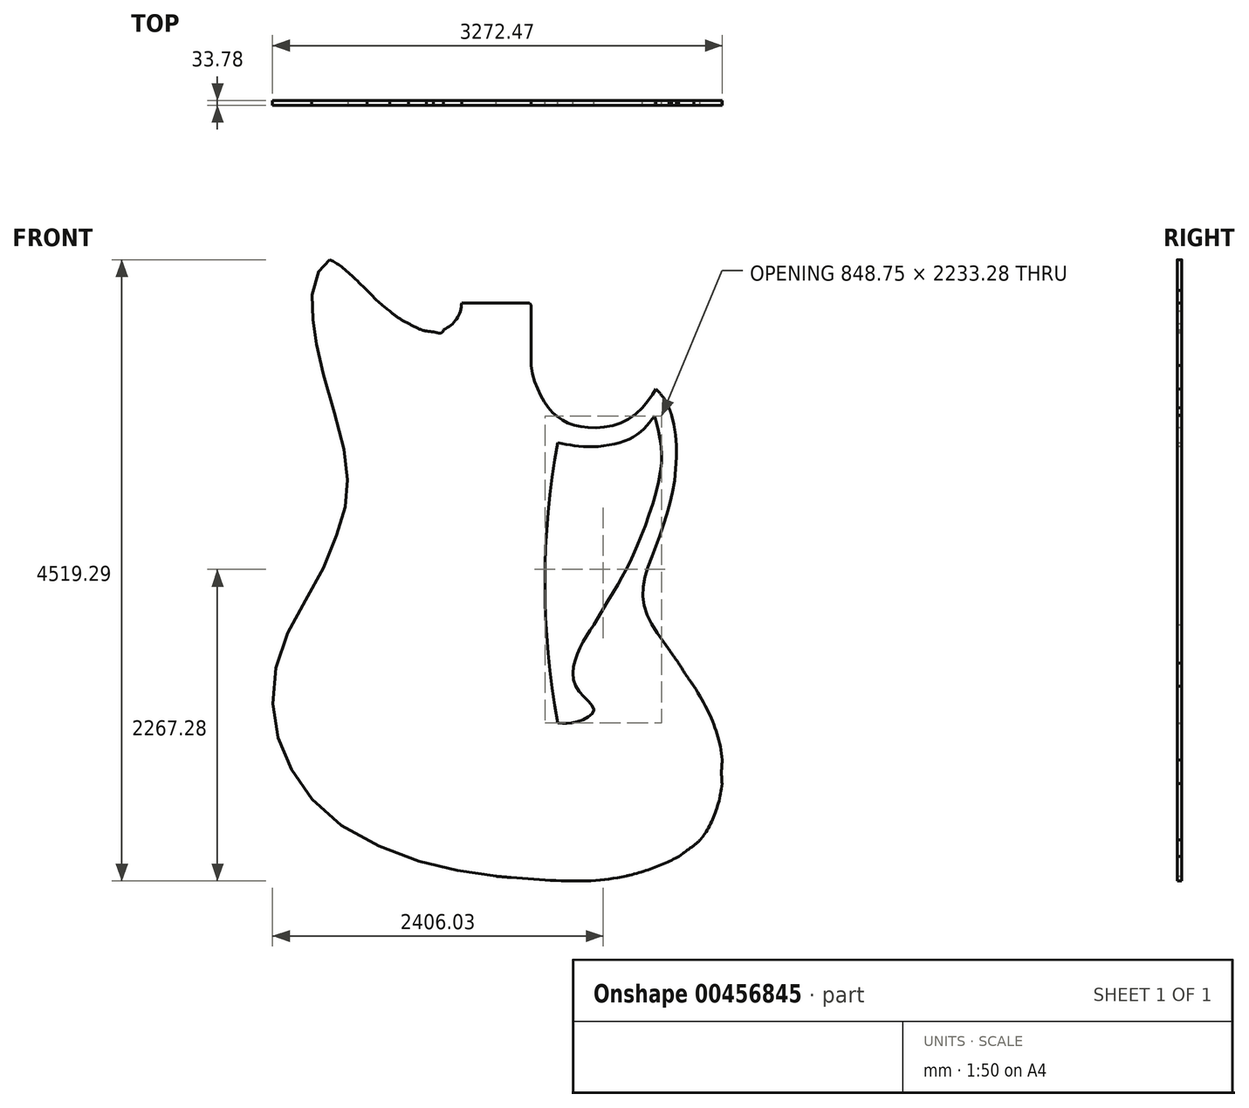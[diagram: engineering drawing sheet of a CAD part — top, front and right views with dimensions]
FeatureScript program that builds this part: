
annotation { "Feature Type Name" : "Feature", "Feature Type Description" : "" }
export const myFeature = defineFeature(function(context is Context, id is Id, definition is map)
    precondition{}
    {
        {
            var Q0;
            Q0=qCreatedBy(makeId("Front.planeOp"),FACE);
            var sketch = newSketch(context, id + "F0", { "sketchPlane" : qUnion([Q0])});
            skLineSegment(sketch, "E0", {"start": v(-6299.76, -3394.28) * mm, "end": v(-6299.76, -2656.01) * mm});
            skLineSegment(sketch, "E1", {"start": v(-6805.5, -2914.73) * mm, "end": v(-6805.5, -2630.61) * mm});
            skLineSegment(sketch, "E2", {"start": v(-6552.45, -2630.61) * mm, "end": v(-6552.45, -3394.86) * mm});
            skLineSegment(sketch, "E3", {"start": v(-6805.5, -3394.86) * mm, "end": v(-6805.5, -3072.04) * mm});
            skFitSpline(sketch, "E4", {"points": [v(-5276.05, -3449.11) * mm, v(-5287.3, -3419.3) * mm, v(-5308.03, -3364.3) * mm, v(-5355.3, -3290.17) * mm, v(-5416.6, -3231.95) * mm, v(-5491.73, -3195.94) * mm, v(-5588.2, -3145.91) * mm, v(-5719.98, -3168.37) * mm, v(-5802.47, -3218.14) * mm, v(-5845.07, -3228.05) * mm]});
            skFitSpline(sketch, "E5", {"points": [v(-5044.53, -6506.04) * mm, v(-5026.22, -6487.87) * mm, v(-4988.8, -6419.72) * mm, v(-4934.12, -6297.37) * mm, v(-4910.03, -6158) * mm, v(-4914.3, -6040.1) * mm, v(-4908, -5864.95) * mm, v(-4992.35, -5604.02) * mm, v(-5156.6, -5361.57) * mm, v(-5252.66, -5210.81) * mm, v(-5288.38, -5164.45) * mm]});
            skFitSpline(sketch, "E6", {"points": [v(-5582.6, -6794.39) * mm, v(-5525.91, -6781.71) * mm, v(-5422.3, -6758.55) * mm, v(-5280.26, -6694.9) * mm, v(-5158.48, -6609.42) * mm, v(-5078.14, -6546.43) * mm, v(-5044.53, -6506.04) * mm]});
            skFitSpline(sketch, "E7", {"points": [v(-6513.44, -6803.92) * mm, v(-6430.08, -6813.24) * mm, v(-6198.84, -6839.12) * mm, v(-5885.83, -6842.47) * mm, v(-5659.6, -6811.31) * mm, v(-5582.6, -6794.39) * mm]});
            skLineSegment(sketch, "E8", {"start": v(-6552.45, -6802.18) * mm, "end": v(-6552.45, -3394.86) * mm});
            skLineSegment(sketch, "E9", {"start": v(-6805.5, -3394.86) * mm, "end": v(-6299.4, -3394.86) * mm});
            skLineSegment(sketch, "E10", {"start": v(-6805.5, -3085.71) * mm, "end": v(-6829.62, -3072.04) * mm});
            skLineSegment(sketch, "E11", {"start": v(-6325.16, -2630.61) * mm, "end": v(-6805.5, -2630.61) * mm});
            skLineSegment(sketch, "E12", {"start": v(-6552.45, -3012.74) * mm, "end": v(-6552.45, -2630.61) * mm});
            skFitSpline(sketch, "E13", {"points": [v(-7676.8, -2286.7) * mm, v(-7695.14, -2283.28) * mm, v(-7735.83, -2290.19) * mm, v(-7763.38, -2317.11) * mm, v(-7777.56, -2329.88) * mm]});
            skFitSpline(sketch, "E14", {"points": [v(-6552.45, -6802.18) * mm, v(-7122.24, -6690.77) * mm, v(-7726.89, -6397.1) * mm, v(-8053.7, -6007.88) * mm, v(-8178.3, -5586.4) * mm, v(-8106.52, -5110.04) * mm, v(-7862.77, -4657.97) * mm, v(-7687.73, -4243.4) * mm, v(-7635.05, -3965.52) * mm, v(-7685.82, -3593.24) * mm, v(-7834.6, -3064.8) * mm, v(-7881.52, -2796.52) * mm, v(-7892.2, -2569.59) * mm, v(-7834.6, -2376.3) * mm, v(-7765.47, -2318.94) * mm, v(-7285.71, -2724.93) * mm, v(-7025.82, -2835.37) * mm, v(-6937.48, -2806.54) * mm, v(-6805.5, -2630.61) * mm], "startDerivative": vector(-8367.9, 1054.47) * mm, "endDerivative": vector(19439.29, -15558.9) * mm});
            skPoint(sketch, "E15.17.internal.snap0", {"position": v(-6254.8, -7225.1) * mm});
            skFitSpline(sketch, "E15", {"points": [v(-6552.45, -6802.18) * mm, v(-5969.39, -6837.11) * mm, v(-5582.6, -6794.39) * mm, v(-5249.83, -6671.29) * mm, v(-5044.53, -6506.04) * mm, v(-4915.92, -6170.56) * mm, v(-4928.43, -5832.38) * mm, v(-5044.53, -5540.75) * mm, v(-5288.38, -5164.45) * mm, v(-5485.93, -4796.16) * mm, v(-5390.99, -4398.41) * mm, v(-5254.92, -3911.55) * mm, v(-5276.05, -3449.11) * mm, v(-5391.06, -3257.77) * mm, v(-5558.7, -3166.06) * mm, v(-5784.71, -3206.46) * mm, v(-6012.82, -3259.28) * mm, v(-6254.8, -3158.3) * mm, v(-6296.95, -3091.35) * mm], "startDerivative": vector(8213.16, -709.74) * mm, "endDerivative": vector(-887.98, 2353.13) * mm});
            skFitSpline(sketch, "E16.trimOffspring", {"points": [v(-6552.45, -6802.18) * mm, v(-5969.39, -6837.11) * mm, v(-5582.6, -6794.39) * mm, v(-5249.83, -6671.29) * mm, v(-5044.53, -6506.04) * mm, v(-4915.92, -6170.56) * mm, v(-4928.43, -5832.38) * mm, v(-5044.53, -5540.75) * mm, v(-5288.38, -5164.45) * mm, v(-5485.93, -4796.16) * mm, v(-5390.99, -4398.41) * mm, v(-5254.92, -3911.55) * mm, v(-5276.05, -3449.11) * mm, v(-5391.06, -3257.77) * mm, v(-5558.7, -3166.06) * mm, v(-5784.71, -3206.46) * mm, v(-6012.82, -3259.28) * mm, v(-6254.8, -3158.3) * mm, v(-6296.95, -3091.35) * mm], "startDerivative": vector(8213.16, -709.74) * mm, "endDerivative": vector(-887.98, 2353.13) * mm});
            skFitSpline(sketch, "E17.trimOffspring", {"points": [v(-5044.53, -6506.04) * mm, v(-5026.22, -6487.87) * mm, v(-4988.8, -6419.72) * mm, v(-4934.12, -6297.37) * mm, v(-4910.03, -6158) * mm, v(-4914.3, -6040.1) * mm, v(-4908, -5864.95) * mm, v(-4992.35, -5604.02) * mm, v(-5156.6, -5361.57) * mm, v(-5252.66, -5210.81) * mm, v(-5288.38, -5164.45) * mm]});
            skArc(sketch, "E18.filletArc", {"start": v(-6813.35, -2920.9) * mm, "mid": v(-6807.93, -2919.72) * mm, "end": v(-6805.5, -2914.73) * mm});
            skArc(sketch, "E19", {"start": v(-7062, -2835.37) * mm, "mid": v(-6884.48, -2794.71) * mm, "end": v(-6805.5, -2630.61) * mm});
            skFitSpline(sketch, "E20", {"points": [v(-6299.76, -3085.86) * mm, v(-6209.62, -3342) * mm, v(-6080.38, -3479.85) * mm, v(-5890.06, -3537.13) * mm, v(-5592.72, -3477.35) * mm, v(-5391.06, -3257.77) * mm], "startDerivative": vector(186.4, -1403.01) * mm, "endDerivative": vector(492.18, 886.21) * mm});
            skArc(sketch, "E21.filletArc", {"start": v(-6299.76, -2656.01) * mm, "mid": v(-6307.2, -2638.05) * mm, "end": v(-6325.16, -2630.61) * mm});
            skFitSpline(sketch, "E22", {"points": [v(-7676.8, -2286.7) * mm, v(-7516.18, -2512.91) * mm, v(-7285.71, -2722.08) * mm, v(-7062, -2835.37) * mm], "startDerivative": vector(593.9, -835.52) * mm, "endDerivative": vector(356.24, -9.07) * mm});
            skFitSpline(sketch, "E23", {"points": [v(-5400.32, -3453.2) * mm, v(-5353.84, -3817.3) * mm, v(-5555.25, -4460.28) * mm, v(-5844.1, -4973.14) * mm], "startDerivative": vector(337.74, -1395.2) * mm, "endDerivative": vector(-1351.1, -2298.33) * mm});
            skFitSpline(sketch, "E24", {"points": [v(-5400.32, -3453.2) * mm, v(-5558.7, -3608.13) * mm, v(-5872.87, -3677.86) * mm, v(-6105.28, -3646.87) * mm], "startDerivative": vector(-423.79, -559.11) * mm, "endDerivative": vector(-680.19, 146.8) * mm});
            skFitSpline(sketch, "E25", {"points": [v(-5844.1, -4973.14) * mm, v(-5969.39, -5198.93) * mm, v(-5969.39, -5431.33) * mm, v(-5844.1, -5594.02) * mm, v(-5969.39, -5679.23) * mm, v(-6105.28, -5686) * mm], "startDerivative": vector(-617.68, -938.91) * mm, "endDerivative": vector(-744.7, 59.22) * mm});
            skArc(sketch, "E26", {"start": v(-6105.28, -3646.87) * mm, "mid": v(-6199.6, -4666.44) * mm, "end": v(-6105.28, -5686) * mm});
            skSolve(sketch);
        }
        {
            var Q0;
            Q0=makeQuery(id+"F0.imprint","IMPRINT",FACE,{"disambiguationData":[TD([[makeQuery(id+"F0.imprint","IMPRINT",EDGE,{"derivedFrom":sQuery(id+"F0.wireOp",EDGE,"E2")}),-1.0]])]});
            var Q1;
            Q1=makeQuery(id+"F0.imprint","IMPRINT",FACE,{"disambiguationData":[TD([[makeQuery(id+"F0.imprint","IMPRINT",EDGE,{"derivedFrom":sQuery(id+"F0.wireOp",EDGE,"E2")}),1.0]])]});
            extrude(context, id + "F1", {"entities" : qUnion([Q0, Q1]), "depth" : 33.78 * mm});
        }
    });
